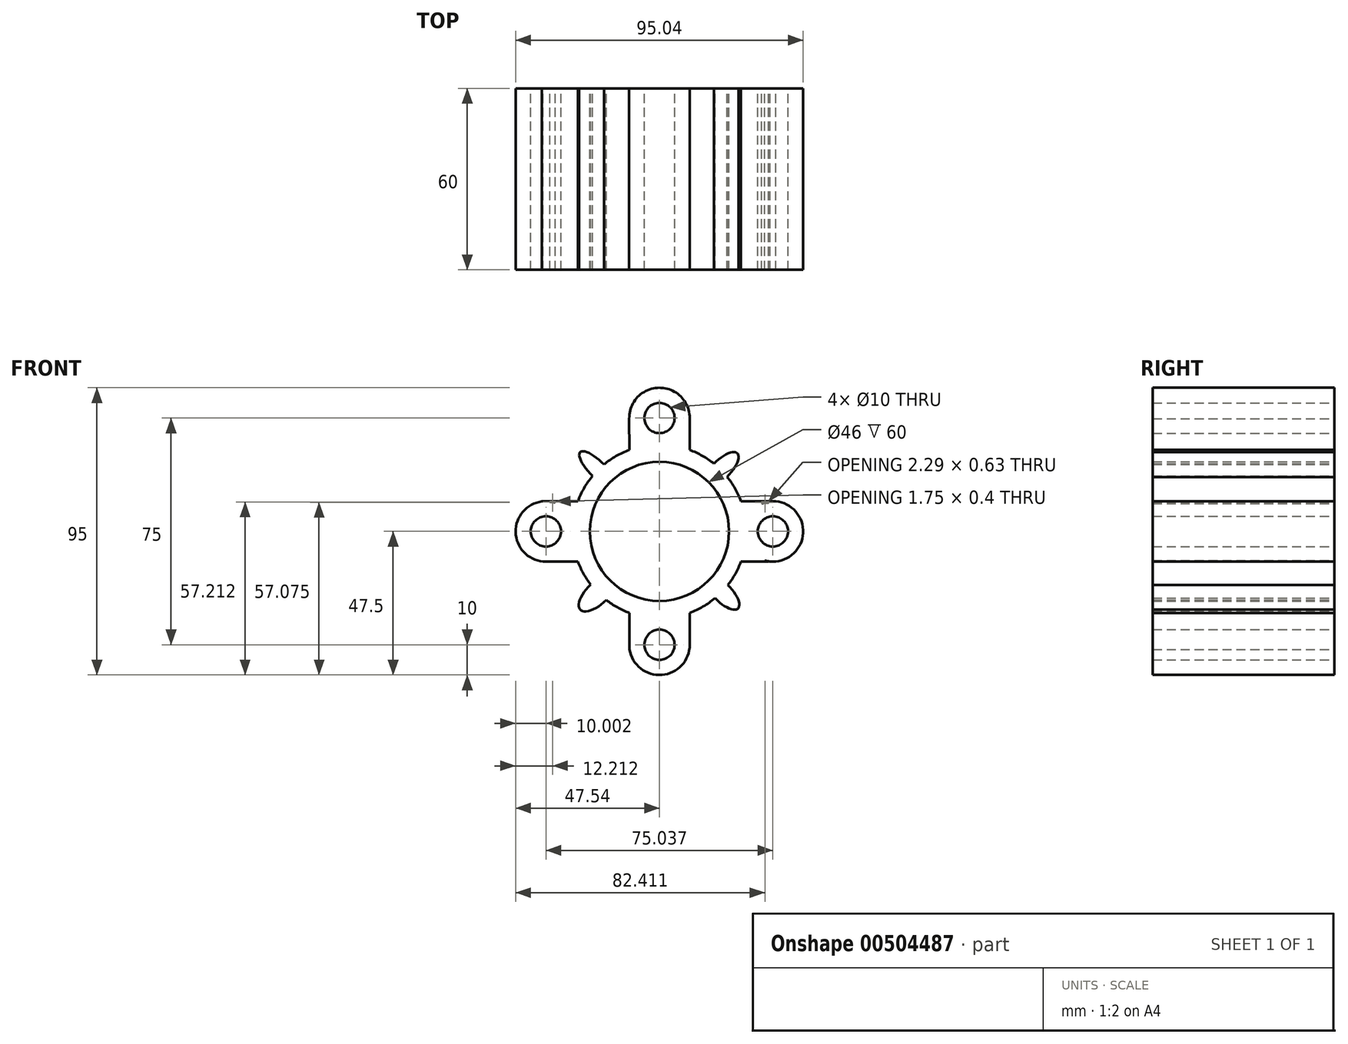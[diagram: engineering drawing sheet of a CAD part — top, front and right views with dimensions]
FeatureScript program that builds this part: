
annotation { "Feature Type Name" : "Feature", "Feature Type Description" : "" }
export const myFeature = defineFeature(function(context is Context, id is Id, definition is map)
    precondition{}
    {
        {
            var Q0;
            Q0=qCreatedBy(makeId("Front.planeOp"),FACE);
            var sketch = newSketch(context, id + "F0", { "sketchPlane" : qUnion([Q0])});
            skCircle(sketch, "E0", {"center": v(0, 0) * mm, "radius": 23 * mm});
            skCircle(sketch, "E1", {"center": v(0, 37.5) * mm, "radius": 5 * mm});
            skCircle(sketch, "E2", {"center": v(37.5, 0) * mm, "radius": 5 * mm});
            skCircle(sketch, "E3", {"center": v(0, -37.5) * mm, "radius": 5 * mm});
            skPoint(sketch, "E4.center.orphan", {"position": v(-32.5, 0) * mm});
            skCircle(sketch, "E5", {"center": v(-37.54, 0) * mm, "radius": 5 * mm});
            skArc(sketch, "E6", {"start": v(-34.45, 9.51) * mm, "mid": v(-47.48, 1.11) * mm, "end": v(-36.63, -9.96) * mm});
            skArc(sketch, "E7", {"start": v(10, 37.5) * mm, "mid": v(-0.1, 47.5) * mm, "end": v(-10, 37.3) * mm});
            skArc(sketch, "E8", {"start": v(34.83, -9.64) * mm, "mid": v(47.48, 0.58) * mm, "end": v(33.73, 9.26) * mm});
            skArc(sketch, "E9", {"start": v(-9.89, -36) * mm, "mid": v(-0.75, -47.47) * mm, "end": v(10, -37.5) * mm});
            skPoint(sketch, "E10", {"position": v(-4.99, 37.17) * mm});
            skPoint(sketch, "E11", {"position": v(4.99, 37.17) * mm});
            skPoint(sketch, "E12", {"position": v(37.17, 4.99) * mm});
            skPoint(sketch, "E13", {"position": v(37.17, -4.99) * mm});
            skPoint(sketch, "E14", {"position": v(4.99, -37.17) * mm});
            skPoint(sketch, "E15", {"position": v(-4.99, -37.17) * mm});
            skPoint(sketch, "E16", {"position": v(-37.2, -4.99) * mm});
            skPoint(sketch, "E17", {"position": v(-37.2, 4.99) * mm});
            skPoint(sketch, "E18", {"position": v(-36.2, 9.91) * mm});
            skLineSegment(sketch, "E19", {"start": v(34.83, -9.64) * mm, "end": v(37.16, -10.28) * mm});
            skArc(sketch, "E20", {"start": v(-36.2, 9.91) * mm, "mid": v(-35.33, 9.7) * mm, "end": v(-34.45, 9.51) * mm});
            skLineSegment(sketch, "E21.trimOffspring", {"start": v(33.73, 9.26) * mm, "end": v(36.01, 9.89) * mm});
            skLineSegment(sketch, "E22", {"start": v(-38.87, 9.91) * mm, "end": v(-26.96, 9.92) * mm});
            skLineSegment(sketch, "E23", {"start": v(-38.44, -9.96) * mm, "end": v(-26.95, -9.96) * mm});
            skLineSegment(sketch, "E24", {"start": v(-10, 37.3) * mm, "end": v(-9.98, 26.94) * mm});
            skLineSegment(sketch, "E25", {"start": v(10, 37.5) * mm, "end": v(10, 26.94) * mm});
            skArc(sketch, "E26", {"start": v(-22.13, 18.32) * mm, "mid": v(-24.9, 14.33) * mm, "end": v(-26.96, 9.92) * mm});
            skLineSegment(sketch, "E27", {"start": v(-9.94, 9.94) * mm, "end": v(-9.96, 9.96) * mm});
            skLineSegment(sketch, "E28", {"start": v(10, -9.71) * mm, "end": v(10.25, -9.96) * mm});
            skLineSegment(sketch, "E29", {"start": v(9.97, 9.97) * mm, "end": v(10, 10) * mm});
            skLineSegment(sketch, "E30", {"start": v(-9.93, -9.93) * mm, "end": v(-9.96, -9.96) * mm});
            skEllipticalArc(sketch, "E31", {});
            skEllipticalArc(sketch, "E32", {});
            skEllipticalArc(sketch, "E33", {});
            skEllipticalArc(sketch, "E34", {});
            skPoint(sketch, "E35", {"position": v(-18.32, 22.14) * mm});
            skPoint(sketch, "E36", {"position": v(-22.22, 18.4) * mm});
            skPoint(sketch, "E37", {"position": v(-22.8, -17.47) * mm});
            skPoint(sketch, "E37.positionSnap0", {"position": v(-22.8, -17.7) * mm});
            skPoint(sketch, "E38", {"position": v(-18.32, -22.14) * mm});
            skPoint(sketch, "E39", {"position": v(18.36, -22.1) * mm});
            skPoint(sketch, "E40", {"position": v(22.63, -17.7) * mm});
            skPoint(sketch, "E41", {"position": v(22.38, 18.02) * mm});
            skPoint(sketch, "E42", {"position": v(18.03, 22.37) * mm});
            skPoint(sketch, "E43", {"position": v(-26.96, 9.92) * mm});
            skPoint(sketch, "E44", {"position": v(-9.98, 26.94) * mm});
            skPoint(sketch, "E45", {"position": v(10, 26.94) * mm});
            skPoint(sketch, "E46", {"position": v(26.94, 9.99) * mm});
            skPoint(sketch, "E47", {"position": v(26.95, -9.96) * mm});
            skPoint(sketch, "E48", {"position": v(10, -26.94) * mm});
            skPoint(sketch, "E49", {"position": v(-9.9, -26.97) * mm});
            skPoint(sketch, "E50", {"position": v(-26.95, -9.96) * mm});
            skPoint(sketch, "E51.trimOffspring.end.orphan", {"position": v(-26.21, 26.22) * mm});
            skLineSegment(sketch, "E52.trimOffspring", {"start": v(-9.96, 9.96) * mm, "end": v(-9.96, 9.94) * mm});
            skLineSegment(sketch, "E53.trimOffspring", {"start": v(10, 20.71) * mm, "end": v(10, -20.71) * mm});
            skArc(sketch, "E54.trimOffspring", {"start": v(18.03, 22.37) * mm, "mid": v(14.2, 24.98) * mm, "end": v(10, 26.94) * mm});
            skArc(sketch, "E55.trimOffspring", {"start": v(-9.98, 26.94) * mm, "mid": v(-14.35, 24.9) * mm, "end": v(-18.32, 22.14) * mm});
            skLineSegment(sketch, "E56.trimOffspring", {"start": v(-9.96, 9.94) * mm, "end": v(-9.94, 9.94) * mm});
            skLineSegment(sketch, "E57.trimOffspring", {"start": v(-9.96, -9.96) * mm, "end": v(-9.93, -9.96) * mm});
            skLineSegment(sketch, "E58.trimOffspring", {"start": v(-9.9, -26.97) * mm, "end": v(-9.88, -39.03) * mm});
            skLineSegment(sketch, "E59.trimOffspring", {"start": v(10, -26.94) * mm, "end": v(10, -37.5) * mm});
            skLineSegment(sketch, "E60.trimOffspring", {"start": v(26.95, -9.96) * mm, "end": v(38.4, -9.96) * mm});
            skLineSegment(sketch, "E61.trimOffspring", {"start": v(26.94, 9.99) * mm, "end": v(37.49, 10) * mm});
            skLineSegment(sketch, "E62.trimOffspring", {"start": v(9.97, 9.97) * mm, "end": v(10, 9.97) * mm});
            skLineSegment(sketch, "E63.trimOffspring", {"start": v(-9.93, -9.93) * mm, "end": v(-9.93, -9.96) * mm});
            skLineSegment(sketch, "E64.trimOffspring", {"start": v(10, -9.96) * mm, "end": v(10.25, -9.96) * mm});
            skArc(sketch, "E65.trimOffspring", {"start": v(-26.95, -9.96) * mm, "mid": v(-25.12, -13.94) * mm, "end": v(-22.71, -17.6) * mm});
            skArc(sketch, "E66.trimOffspring", {"start": v(26.94, 9.99) * mm, "mid": v(24.98, 14.2) * mm, "end": v(22.38, 18.02) * mm});
            skArc(sketch, "E67.trimOffspring", {"start": v(10, -26.94) * mm, "mid": v(14.38, -24.87) * mm, "end": v(18.36, -22.1) * mm});
            skArc(sketch, "E68.trimOffspring", {"start": v(-18.32, -22.14) * mm, "mid": v(-14.31, -24.91) * mm, "end": v(-9.9, -26.97) * mm});
            skArc(sketch, "E69.trimOffspring", {"start": v(22.63, -17.7) * mm, "mid": v(25.1, -14) * mm, "end": v(26.95, -9.96) * mm});
            const initialGuessF0  = {"E31": [-0.02031530027365176, 0.020317091746848225, -0.7070756043173808, 0.7071379566811633, 0.00834081343801919, 0.002699407057115495, 4.697154826808392, 1.5860304803711944], "E32": [0.020317091746848228, 0.020315300273651762, 0.6959552261895693, 0.718085178192271, 0.0077384353821595645, 0.003074471263300185, 4.684806738298111, 1.5858475224248245], "E33": [0.02060919430981291, -0.02001890986439718, 0.6999099133073541, -0.7142311343354419, 0.007647190538562919, 0.0030684203532637846, 4.700835351425029, 1.6022341209173774], "E34": [-0.020317091746848225, -0.02031530027365176, -0.7246788995119215, -0.6890867090593101, 0.008054264905837015, 0.003617633999785932, 4.695355881181577, 1.6105486796098472]};
            skSetInitialGuess(sketch, initialGuessF0);
            skSolve(sketch);
        }
        {
            var Q0;
            Q0=makeQuery(id+"F0.imprint","IMPRINT",FACE,{"disambiguationData":[TD([[makeQuery(id+"F0.imprint","IMPRINT",EDGE,{"derivedFrom":sQuery(id+"F0.wireOp",EDGE,"E1")}),-1.0]])]});
            extrude(context, id + "F1", {"entities" : qUnion([Q0]), "depth" : 60 * mm});
        }
    });
